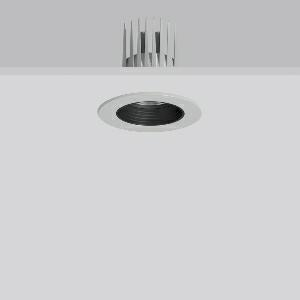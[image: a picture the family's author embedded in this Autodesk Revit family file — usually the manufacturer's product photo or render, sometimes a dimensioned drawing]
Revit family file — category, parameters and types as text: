
# Revit family: heledon_mini_e_901754_004_76_6760
name_source: partatom
category: Lighting Fixtures
units: mm (PartAtom-declared; Revit-internal decimal feet)

## family parameters
Cut with Voids When Loaded = No
Host = Face
Light Source = No
Part Type = Normal
Room Calculation Point = No
Round Connector Dimension = Use Diameter
Shared = No

## types (1)
- HELEDON mini E (1 x LED Modul 930, 3250 lm, 3000)
    Apparent Load = 29 VA
    Approval mark = CE
    CIE Flux Codes = 80 99 100 100 100
    Color Rendering = 90
    Color Temperature = 3000
    Default Elevation = 1800 mm
    Description = Series: HELEDON mini
Round recessed downlight. Housing: die-cast aluminium, powder-coated. Black plastic ring and recessed LED to prevent glare from the side. Optical assembly with lens made of plastic (polycarbonate) for the best homogeneous light distribution - can be changed without tools. Best colour rendering index Ra>90. Suitable for Recessed ceiling mounting. Installation without tools thanks to spring fastening system. Including separate LED converter with connecting cable 600 mm.High quality converter without flickering and stroboscopic effect. Through-wiring box (5 pole) available as accessory. The following accessories can be mounted without use of tools: interchangeable lenses, decorative glasses, honeycomb louvre, clear and frosted diffusers, white interchangeable plastic ring. 
Colour: silver
Diameter: 124 mm
Height: 3 mm
Cut-out diameter: 114 mm
Recess height: 170 mm
Luminaire: recess height: 120 mm
Lamp: LED
Socket: without socket
Colour temperature: 3000K
Colour rendering index (CRI): 92
System power: 29 W
Rated luminous flux: 3250 lm
Luminous efficiency: 112 lm/W
Control gear: Converter, dimmable, DALI
Protection class: II
Type of protection: IP 20
    Height = 0 mm  [stored 0 ft]
    Lamp = 1 x LED Modul 930
    Lamp Light Flux = 3250 lm
    Lamp count = 1
    Length = 124 mm  [stored 0.406824 ft]
    Lifetime = 50000 h
    Luminous efficacy = 112 lm/W
    Manufacturer = RZB
    ModVariant = No
    Model = 901754.004.76
    Mounting Place = Ceiling
    Mounting Type = Recessed
    Number of Poles = 1
    OnlyDefault = Yes
    Power Factor = 1
    Product Name = HELEDON mini E
    Product group = Recessed downlights
    ProductGroupID = 402
    Protection Class = Protection class II
    Protection Degree = IP 20
    RLX_Detail_Level = 1
    RLX_Emergency_Light_Flux = 0 lm
    RLX_Emergency_Type = 0
    RLX_Emergency_Type_DB = No
    RlxData = <blob elided: 125849 chars, md5=504cbe1b>
    Socket = socket
    Standby Power = 0 W
    System Light Flux = 3250 lm
    System Power = 29 W
    Type Comments = Product without accessories
    Type Image = 901656.004.jpg
    URL = http://relux.com
    VarID = ---
    Voltage = 230 V
    Voltage Range = 220-240 V
    Weight = 0.00 kg
    Width = 0 mm  [stored 0 ft]

note: [stored X ft] marks values corroborated as IEEE doubles in the binary element streams (Revit-internal decimal feet)

## geometry (parser evidence)
native form markers: Blend x4, Sweep x12
no freeform markers — native parametric forms only
